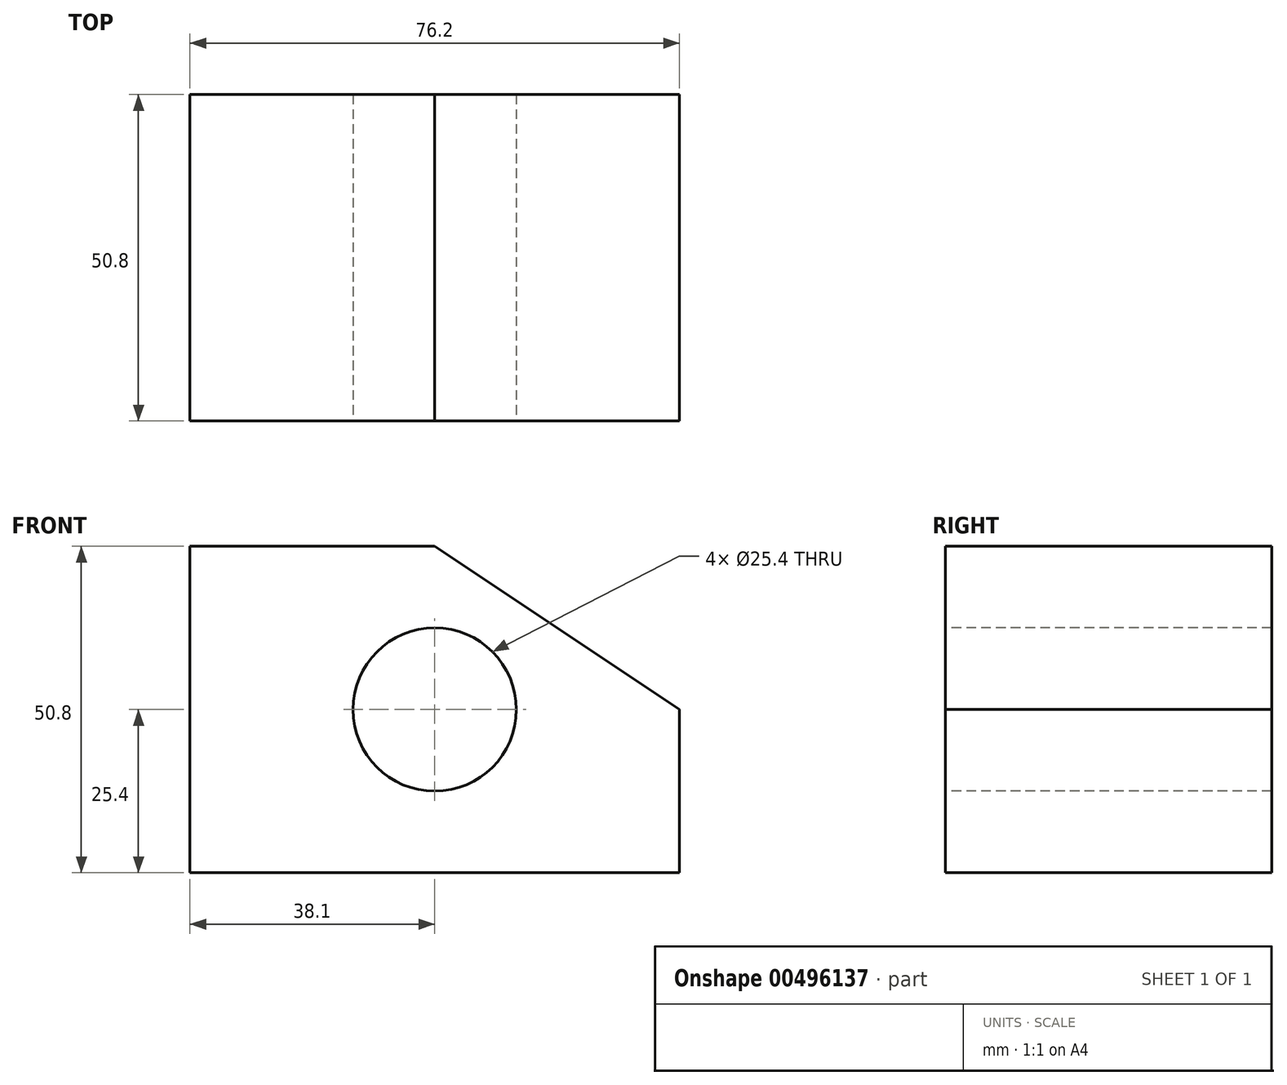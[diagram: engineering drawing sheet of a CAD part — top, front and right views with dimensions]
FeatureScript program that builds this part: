
annotation { "Feature Type Name" : "Feature", "Feature Type Description" : "" }
export const myFeature = defineFeature(function(context is Context, id is Id, definition is map)
    precondition{}
    {
        {
            var Q0;
            Q0=qCreatedBy(makeId("Top.planeOp"),FACE);
            var sketch = newSketch(context, id + "F0", { "sketchPlane" : qUnion([Q0])});
            skLineSegment(sketch, "E0.bottom", {"start": v(38.1, -25.4) * mm, "end": v(-38.1, -25.4) * mm});
            skLineSegment(sketch, "E0.top", {"start": v(38.1, 25.4) * mm, "end": v(-38.1, 25.4) * mm});
            skLineSegment(sketch, "E0.left", {"start": v(38.1, -25.4) * mm, "end": v(38.1, 25.4) * mm});
            skLineSegment(sketch, "E0.right", {"start": v(-38.1, -25.4) * mm, "end": v(-38.1, 25.4) * mm});
            skPoint(sketch, "E0.middle", {"position": v(0, 0) * mm});
            skSolve(sketch);
        }
        {
            var Q0;
            Q0 = qSketchRegion(id + "F0", true);
            extrude(context, id + "F1", {"entities" : qUnion([Q0]), "depth" : 50.8 * mm});
        }
        {
            var Q0;
            Q0=makeQuery(id+"F1.opExtrude","SWEPT_FACE",FACE,{"disambiguationData":[OSD([sQuery(id+"F0.wireOp",EDGE,"E0.bottom")])]});
            var sketch = newSketch(context, id + "F2", { "sketchPlane" : qUnion([Q0])});
            skCircle(sketch, "E1", {"center": v(0, 25.4) * mm, "radius": 12.7 * mm});
            skLineSegment(sketch, "E2", {"start": v(0, 50.8) * mm, "end": v(38.1, 25.4) * mm});
            skSolve(sketch);
        }
        {
            var Q0;
            {var subQ0=sQuery(id+"F2.wireOp",EDGE,"E2");Q0=makeQuery(id+"F2.imprint","IMPRINT",FACE,{"disambiguationData":[TD([[makeQuery(id+"F2.imprint","IMPRINT",EDGE,{"derivedFrom":subQ0}),1.0]])]});}
            extrude(context, id + "F3", {"entities" : qUnion([Q0]), "operationType" : NewBodyOperationType.REMOVE, "oppositeDirection" : true, "depth" : 50.8 * mm});
        }
        {
            var Q0;
            Q0=makeQuery(id+"F2.imprint","IMPRINT",FACE,{"disambiguationData":[TD([[makeQuery(id+"F2.imprint","IMPRINT",EDGE,{"derivedFrom":sQuery(id+"F2.wireOp",EDGE,"E1")}),1.0]])]});
            extrude(context, id + "F4", {"entities" : qUnion([Q0]), "operationType" : NewBodyOperationType.REMOVE, "oppositeDirection" : true, "depth" : 50.8 * mm});
        }
    });
